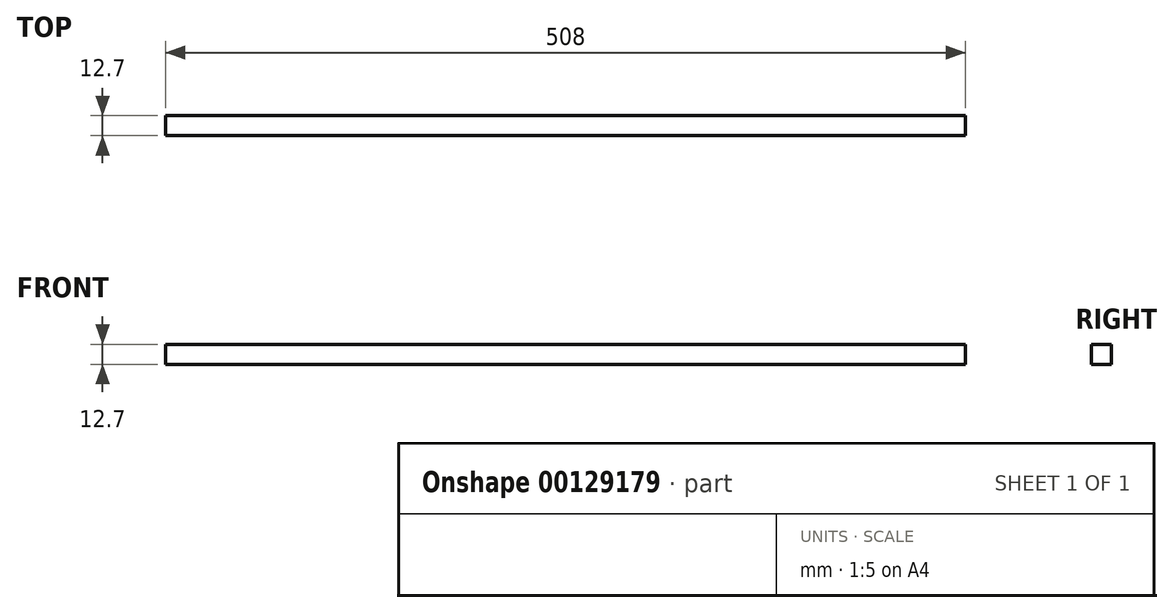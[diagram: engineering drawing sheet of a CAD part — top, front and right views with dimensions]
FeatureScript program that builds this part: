
annotation { "Feature Type Name" : "Feature", "Feature Type Description" : "" }
export const myFeature = defineFeature(function(context is Context, id is Id, definition is map)
    precondition{}
    {
        {
            var Q0;
            Q0=qCreatedBy(makeId("Front.planeOp"),FACE);
            var sketch = newSketch(context, id + "F0", { "sketchPlane" : qUnion([Q0])});
            skLineSegment(sketch, "E0.bottom", {"start": v(254, 6.35) * mm, "end": v(-254, 6.35) * mm});
            skLineSegment(sketch, "E0.top", {"start": v(254, -6.35) * mm, "end": v(-254, -6.35) * mm});
            skLineSegment(sketch, "E0.left", {"start": v(254, 6.35) * mm, "end": v(254, -6.35) * mm});
            skLineSegment(sketch, "E0.right", {"start": v(-254, 6.35) * mm, "end": v(-254, -6.35) * mm});
            skPoint(sketch, "E0.middle", {"position": v(0, 0) * mm});
            skSolve(sketch);
        }
        {
            var Q0;
            Q0 = qSketchRegion(id + "F0", true);
            extrude(context, id + "F1", {"entities" : qUnion([Q0]), "depth" : 12.7 * mm});
        }
    });
